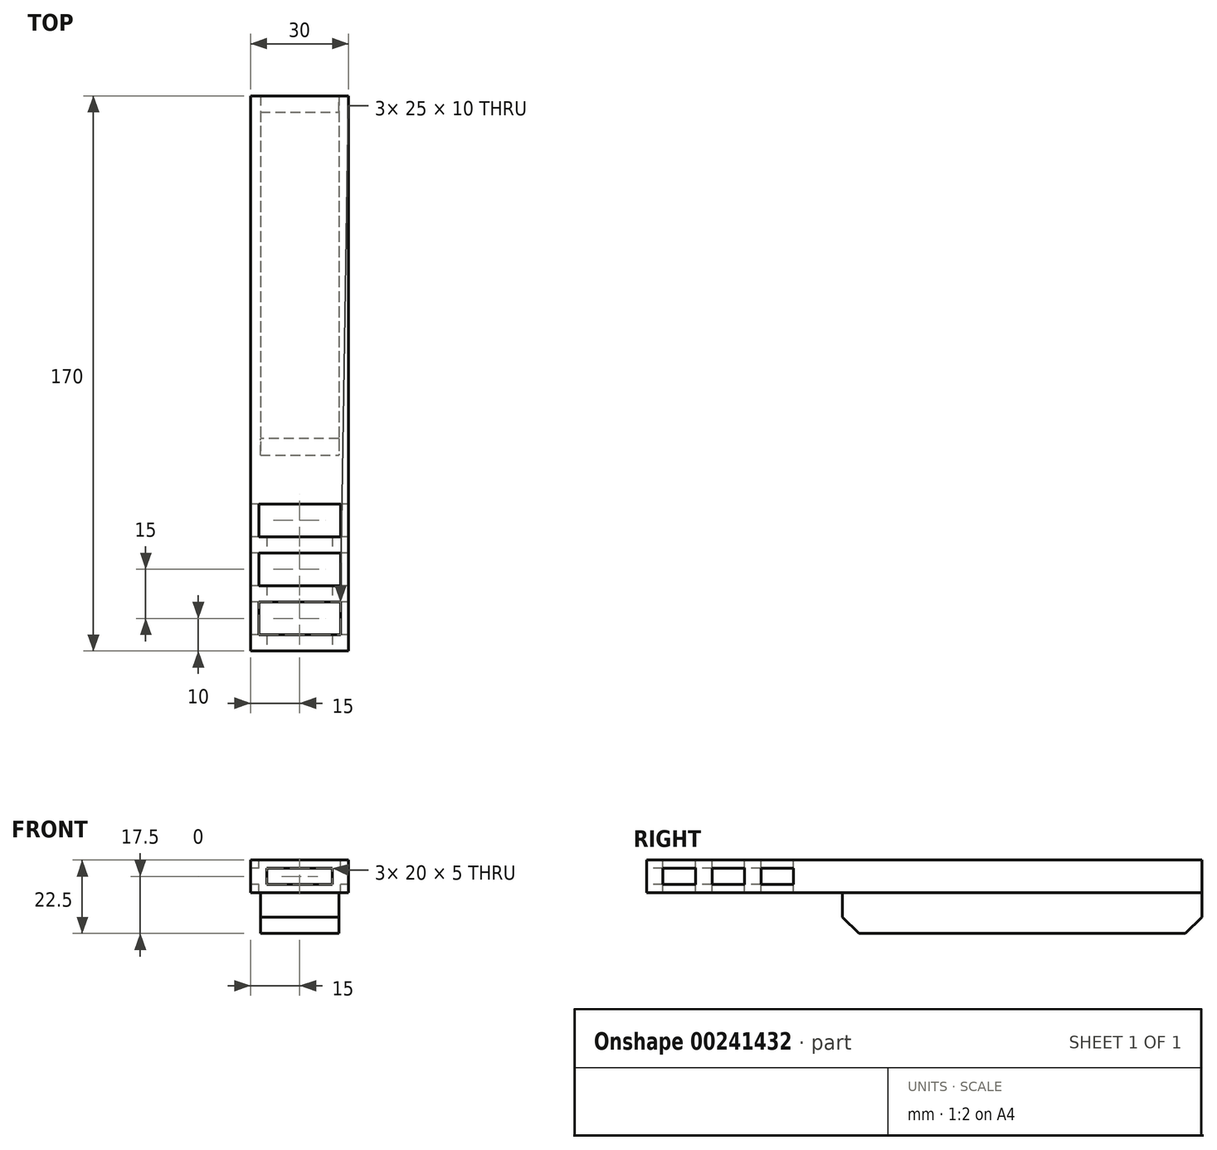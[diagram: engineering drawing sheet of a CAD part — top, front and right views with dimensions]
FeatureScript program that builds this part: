
annotation { "Feature Type Name" : "Feature", "Feature Type Description" : "" }
export const myFeature = defineFeature(function(context is Context, id is Id, definition is map)
    precondition{}
    {
        {
            var Q0;
            Q0=qCreatedBy(makeId("Front.planeOp"),FACE);
            var sketch = newSketch(context, id + "F0", { "sketchPlane" : qUnion([Q0])});
            skLineSegment(sketch, "E0.bottom", {"start": v(-15, 5) * mm, "end": v(15, 5) * mm});
            skLineSegment(sketch, "E0.top", {"start": v(-15, -5) * mm, "end": v(15, -5) * mm});
            skLineSegment(sketch, "E0.left", {"start": v(-15, 5) * mm, "end": v(-15, -5) * mm});
            skLineSegment(sketch, "E0.right", {"start": v(15, 5) * mm, "end": v(15, -5) * mm});
            skPoint(sketch, "E0.middle", {"position": v(0, 0) * mm});
            skSolve(sketch);
        }
        {
            var Q0;
            Q0 = qSketchRegion(id + "F0", true);
            extrude(context, id + "F1", {"entities" : qUnion([Q0]), "depth" : 120 * mm});
        }
        {
            var Q0;
            Q0=makeQuery(id+"F1.opExtrude","CAP_FACE",FACE,{"disambiguationData":[OSD([sQuery(id+"F0.wireOp",EDGE,"E0.bottom"),sQuery(id+"F0.wireOp",EDGE,"E0.top"),sQuery(id+"F0.wireOp",EDGE,"E0.left"),sQuery(id+"F0.wireOp",EDGE,"E0.right")])],"isStart":false});
            var sketch = newSketch(context, id + "F2", { "sketchPlane" : qUnion([Q0])});
            skLineSegment(sketch, "E1.bottom", {"start": v(-15, 5) * mm, "end": v(15, 5) * mm});
            skLineSegment(sketch, "E1.top", {"start": v(-15, -5) * mm, "end": v(15, -5) * mm});
            skLineSegment(sketch, "E1.left", {"start": v(-15, 5) * mm, "end": v(-15, -5) * mm});
            skLineSegment(sketch, "E1.right", {"start": v(15, 5) * mm, "end": v(15, -5) * mm});
            skPoint(sketch, "E1.middle", {"position": v(0, 0) * mm});
            skSolve(sketch);
        }
        {
            var Q0;
            Q0 = qSketchRegion(id + "F2", true);
            extrude(context, id + "F3", {"entities" : qUnion([Q0]), "operationType" : NewBodyOperationType.ADD, "depth" : 50 * mm});
        }
        {
            var Q0;
            Q0=makeQuery(id+"F3.boolean.opBoolean","MERGE",FACE,{"derivedFrom":[makeQuery(id+"F1.opExtrude","SWEPT_FACE",FACE,{"disambiguationData":[OSD([sQuery(id+"F0.wireOp",EDGE,"E0.left")])]}),makeQuery(id+"F3.opExtrude","SWEPT_FACE",FACE,{"disambiguationData":[OSD([sQuery(id+"F2.wireOp",EDGE,"E1.left")])]})]});
            var sketch = newSketch(context, id + "F4", { "sketchPlane" : qUnion([Q0])});
            skLineSegment(sketch, "E2.bottom", {"start": v(165, 2.5) * mm, "end": v(155, 2.5) * mm});
            skLineSegment(sketch, "E2.top", {"start": v(165, -2.5) * mm, "end": v(155, -2.5) * mm});
            skLineSegment(sketch, "E2.left", {"start": v(165, 2.5) * mm, "end": v(165, -2.5) * mm});
            skLineSegment(sketch, "E2.right", {"start": v(155, 2.5) * mm, "end": v(155, -2.5) * mm});
            skLineSegment(sketch, "E3.1.0.0", {"start": v(150, 2.5) * mm, "end": v(140, 2.5) * mm});
            skLineSegment(sketch, "E3.1.0.1", {"start": v(150, -2.5) * mm, "end": v(140, -2.5) * mm});
            skLineSegment(sketch, "E3.1.0.2", {"start": v(150, 2.5) * mm, "end": v(150, -2.5) * mm});
            skLineSegment(sketch, "E3.1.0.3", {"start": v(140, 2.5) * mm, "end": v(140, -2.5) * mm});
            skLineSegment(sketch, "E3.2.0.0", {"start": v(135, 2.5) * mm, "end": v(125, 2.5) * mm});
            skLineSegment(sketch, "E3.2.0.1", {"start": v(135, -2.5) * mm, "end": v(125, -2.5) * mm});
            skLineSegment(sketch, "E3.2.0.2", {"start": v(135, 2.5) * mm, "end": v(135, -2.5) * mm});
            skLineSegment(sketch, "E3.2.0.3", {"start": v(125, 2.5) * mm, "end": v(125, -2.5) * mm});
            skLineSegment(sketch, "E3.direction1", {"start": v(155, -2.5) * mm, "end": v(140, -2.5) * mm, "construction": true});
            skSolve(sketch);
        }
        {
            var Q0;
            Q0 = qSketchRegion(id + "F4", true);
            extrude(context, id + "F5", {"entities" : qUnion([Q0]), "operationType" : NewBodyOperationType.REMOVE, "endBound" : BoundingType.THROUGH_ALL, "oppositeDirection" : true, "depth" : 25 * mm});
        }
        {
            var Q0;
            Q0=makeQuery(id+"F3.boolean.opBoolean","MERGE",FACE,{"derivedFrom":[makeQuery(id+"F1.opExtrude","SWEPT_FACE",FACE,{"disambiguationData":[OSD([sQuery(id+"F0.wireOp",EDGE,"E0.bottom")])]}),makeQuery(id+"F3.opExtrude","SWEPT_FACE",FACE,{"disambiguationData":[OSD([sQuery(id+"F2.wireOp",EDGE,"E1.bottom")])]})]});
            var sketch = newSketch(context, id + "F6", { "sketchPlane" : qUnion([Q0])});
            skLineSegment(sketch, "E4.bottom", {"start": v(-12.5, -165) * mm, "end": v(12.5, -165) * mm});
            skLineSegment(sketch, "E4.top", {"start": v(-12.5, -155) * mm, "end": v(12.5, -155) * mm});
            skLineSegment(sketch, "E4.left", {"start": v(-12.5, -165) * mm, "end": v(-12.5, -155) * mm});
            skLineSegment(sketch, "E4.right", {"start": v(12.5, -165) * mm, "end": v(12.5, -155) * mm});
            skLineSegment(sketch, "E5.0.1.0", {"start": v(-12.5, -150) * mm, "end": v(-12.5, -140) * mm});
            skLineSegment(sketch, "E5.0.1.1", {"start": v(12.5, -150) * mm, "end": v(12.5, -140) * mm});
            skLineSegment(sketch, "E5.0.1.2", {"start": v(-12.5, -150) * mm, "end": v(12.5, -150) * mm});
            skLineSegment(sketch, "E5.0.1.3", {"start": v(-12.5, -140) * mm, "end": v(12.5, -140) * mm});
            skLineSegment(sketch, "E5.0.2.0", {"start": v(-12.5, -135) * mm, "end": v(-12.5, -125) * mm});
            skLineSegment(sketch, "E5.0.2.1", {"start": v(12.5, -135) * mm, "end": v(12.5, -125) * mm});
            skLineSegment(sketch, "E5.0.2.2", {"start": v(-12.5, -135) * mm, "end": v(12.5, -135) * mm});
            skLineSegment(sketch, "E5.0.2.3", {"start": v(-12.5, -125) * mm, "end": v(12.5, -125) * mm});
            skLineSegment(sketch, "E5.direction1", {"start": v(-12.5, -165) * mm, "end": v(12.5, -165) * mm, "construction": true});
            skLineSegment(sketch, "E5.direction2", {"start": v(-12.5, -165) * mm, "end": v(-12.5, -150) * mm, "construction": true});
            skSolve(sketch);
        }
        {
            var Q0;
            Q0 = qSketchRegion(id + "F6", true);
            extrude(context, id + "F7", {"entities" : qUnion([Q0]), "operationType" : NewBodyOperationType.REMOVE, "endBound" : BoundingType.THROUGH_ALL, "oppositeDirection" : true, "depth" : 25 * mm});
        }
        {
            var Q0;
            Q0=makeQuery(id+"F3.opExtrude","CAP_FACE",FACE,{"disambiguationData":[OSD([sQuery(id+"F2.wireOp",EDGE,"E1.bottom"),sQuery(id+"F2.wireOp",EDGE,"E1.top"),sQuery(id+"F2.wireOp",EDGE,"E1.left"),sQuery(id+"F2.wireOp",EDGE,"E1.right")])],"isStart":false});
            var sketch = newSketch(context, id + "F8", { "sketchPlane" : qUnion([Q0])});
            skLineSegment(sketch, "E6.bottom", {"start": v(-10, 2.5) * mm, "end": v(10, 2.5) * mm});
            skLineSegment(sketch, "E6.top", {"start": v(-10, -2.5) * mm, "end": v(10, -2.5) * mm});
            skLineSegment(sketch, "E6.left", {"start": v(-10, 2.5) * mm, "end": v(-10, -2.5) * mm});
            skLineSegment(sketch, "E6.right", {"start": v(10, 2.5) * mm, "end": v(10, -2.5) * mm});
            skSolve(sketch);
        }
        {
            var Q0;
            Q0 = qSketchRegion(id + "F8", true);
            extrude(context, id + "F9", {"entities" : qUnion([Q0]), "operationType" : NewBodyOperationType.REMOVE, "oppositeDirection" : true, "depth" : 45 * mm});
        }
        {
            var Q0;
            Q0=makeQuery(id+"F3.boolean.opBoolean","MERGE",FACE,{"derivedFrom":[makeQuery(id+"F1.opExtrude","SWEPT_FACE",FACE,{"disambiguationData":[OSD([sQuery(id+"F0.wireOp",EDGE,"E0.top")])]}),makeQuery(id+"F3.opExtrude","SWEPT_FACE",FACE,{"disambiguationData":[OSD([sQuery(id+"F2.wireOp",EDGE,"E1.top")])]})]});
            var sketch = newSketch(context, id + "F10", { "sketchPlane" : qUnion([Q0])});
            skLineSegment(sketch, "E7.bottom", {"start": v(-12, 0) * mm, "end": v(12, 0) * mm});
            skLineSegment(sketch, "E7.top", {"start": v(-12, 110) * mm, "end": v(12, 110) * mm});
            skLineSegment(sketch, "E7.left", {"start": v(-12, 0) * mm, "end": v(-12, 110) * mm});
            skLineSegment(sketch, "E7.right", {"start": v(12, 0) * mm, "end": v(12, 110) * mm});
            skSolve(sketch);
        }
        {
            var Q0;
            Q0 = qSketchRegion(id + "F10", true);
            extrude(context, id + "F11", {"entities" : qUnion([Q0]), "operationType" : NewBodyOperationType.ADD, "depth" : 12.5 * mm});
        }
        {
            var Q0;
            Q0=makeQuery(id+"F11.opExtrude","CAP_EDGE",EDGE,{"disambiguationData":[OSD([sQuery(id+"F10.wireOp",EDGE,"E7.top")])],"isStart":false});
            var Q1;
            Q1=makeQuery(id+"F11.opExtrude","CAP_EDGE",EDGE,{"disambiguationData":[OSD([sQuery(id+"F10.wireOp",EDGE,"E7.bottom")])],"isStart":false});
            chamfer(context, id + "F12", {"entities" : qUnion([Q0, Q1]), "width" : 5 * mm, "tangentPropagation" : true});
        }
    });
